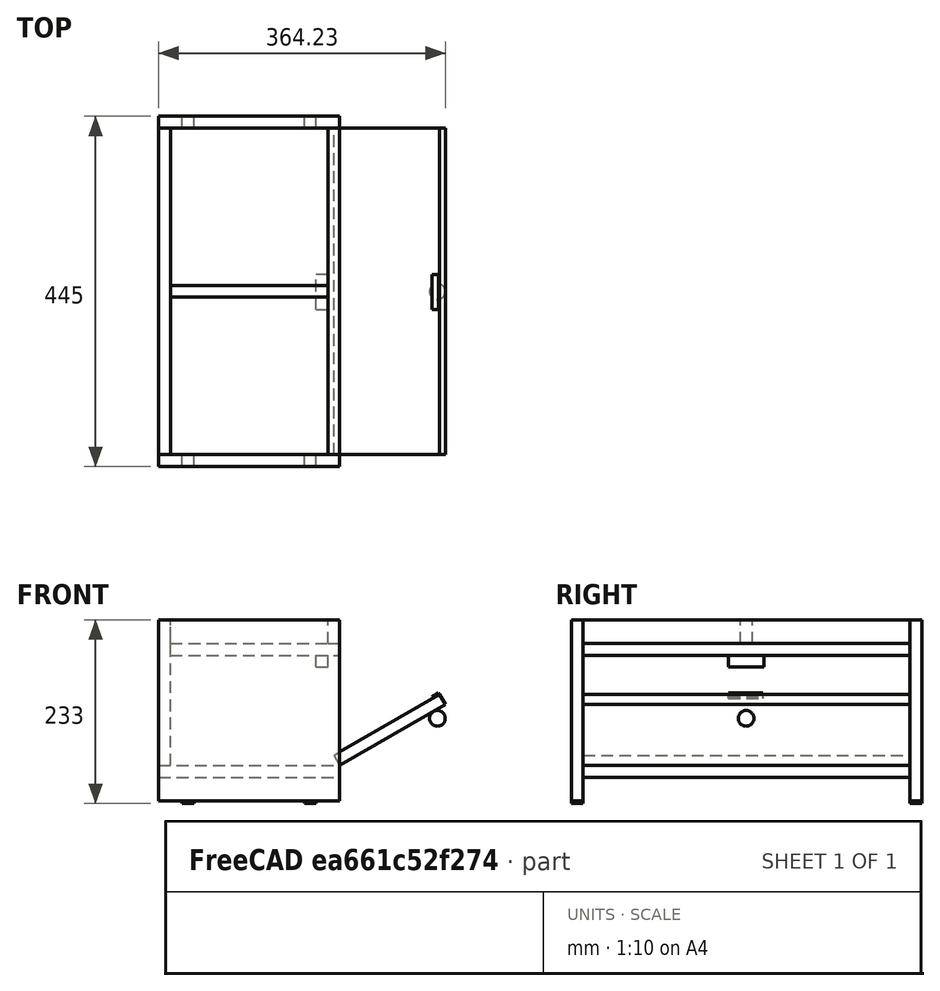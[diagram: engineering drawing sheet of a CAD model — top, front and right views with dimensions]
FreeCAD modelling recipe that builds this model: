
FCSTD DOCUMENT  (FreeCAD 0.17R13522 (Git))
Label: SuporteParaComedouro
License: All rights reserved
LicenseURL: http://en.wikipedia.org/wiki/All_rights_reserved
objects: Part::Box×14, Part::Sphere×1
note: 15 computed .brp shape members not serialized (recipe doc carries the construction recipe); baked Part::Feature solids carry a one-line shape summary decoded from their .brp

FEATURE [Part::Box] Box  label="SuporteLateralVerticalEsquerdo"
  AttacherType = Attacher::AttachEngine3D
  Height = 230
  Length = 230
  Width = 15
FEATURE [Part::Box] Box001  label="TampoSuperiorHorizontal"
  AttacherType = Attacher::AttachEngine3D
  Height = 15
  Length = 215
  Placement = pos=(15,15,185) rot=(0,0,1;0rad)
  Width = 415
FEATURE [Part::Box] Box002  label="SuporteLateralVerticalDireito"
  AttacherType = Attacher::AttachEngine3D
  Height = 230
  Length = 230
  Placement = pos=(0,430,0) rot=(0,0,1;0rad)
  Width = 15
FEATURE [Part::Box] Box003  label="SuporteVerticalMeio"
  AttacherType = Attacher::AttachEngine3D
  Height = 30
  Length = 200
  Placement = pos=(15,215,200) rot=(0,0,1;0rad)
  Width = 15
FEATURE [Part::Box] Box005  label="SuporteFrenteSuperiorVertical"
  AttacherType = Attacher::AttachEngine3D
  Height = 30
  Length = 15
  Placement = pos=(215,15,200) rot=(0,0,1;0rad)
  Width = 415
FEATURE [Part::Box] Box006  label="SuporteFundoInferiorVertical"
  AttacherType = Attacher::AttachEngine3D
  Height = 185
  Length = 15
  Placement = pos=(0,15,45) rot=(0,0,1;0rad)
  Width = 415
FEATURE [Part::Box] Box007  label="TampoInferiorHorizontal"
  AttacherType = Attacher::AttachEngine3D
  Height = 15
  Length = 230
  Placement = pos=(0,15,30) rot=(0,0,1;0rad)
  Width = 415
FEATURE [Part::Box] Box008  label="TampaBasculante"
  AttacherType = Attacher::AttachEngine3D
  Height = 155
  Length = 15
  Placement = pos=(222.5,15,58) rot=(0,1,0;1.0472rad)
  Width = 415
FEATURE [Part::Box] Box010  label="ImaDaMesa SuperiorHorizontal"
  AttacherType = Attacher::AttachEngine3D
  Height = 15
  Length = 15
  Placement = pos=(200,199.5,170) rot=(0,0,1;0rad)
  Width = 45
FEATURE [Part::Box] Box011  label="ChapaDoIma"
  AttacherType = Attacher::AttachEngine3D
  Height = 10
  Length = 2
  Placement = pos=(347,199.5,132) rot=(0,1,0;1.0472rad)
  Width = 44
FEATURE [Part::Sphere] Sphere  label="Puxador"
  Angle1 = -90
  Angle2 = 90
  Angle3 = 360
  AttacherType = Attacher::AttachEngine3D
  Placement = pos=(354,222,105) rot=(0,0,1;0rad)
  Radius = 10
FEATURE [Part::Box] Box012  label="Cube"
  AttacherType = Attacher::AttachEngine3D
  Height = 3
  Length = 15
  Placement = pos=(30,0,-3) rot=(0,0,1;0rad)
  Width = 15
FEATURE [Part::Box] Box013  label="Cube001"
  AttacherType = Attacher::AttachEngine3D
  Height = 3
  Length = 15
  Placement = pos=(185,0,-3) rot=(0,0,1;0rad)
  Width = 15
FEATURE [Part::Box] Box014  label="Cube002"
  AttacherType = Attacher::AttachEngine3D
  Height = 3
  Length = 15
  Placement = pos=(30,430,-3) rot=(0,0,1;0rad)
  Width = 15
FEATURE [Part::Box] Box015  label="Cube003"
  AttacherType = Attacher::AttachEngine3D
  Height = 3
  Length = 15
  Placement = pos=(185,430,-3) rot=(0,0,1;0rad)
  Width = 15
